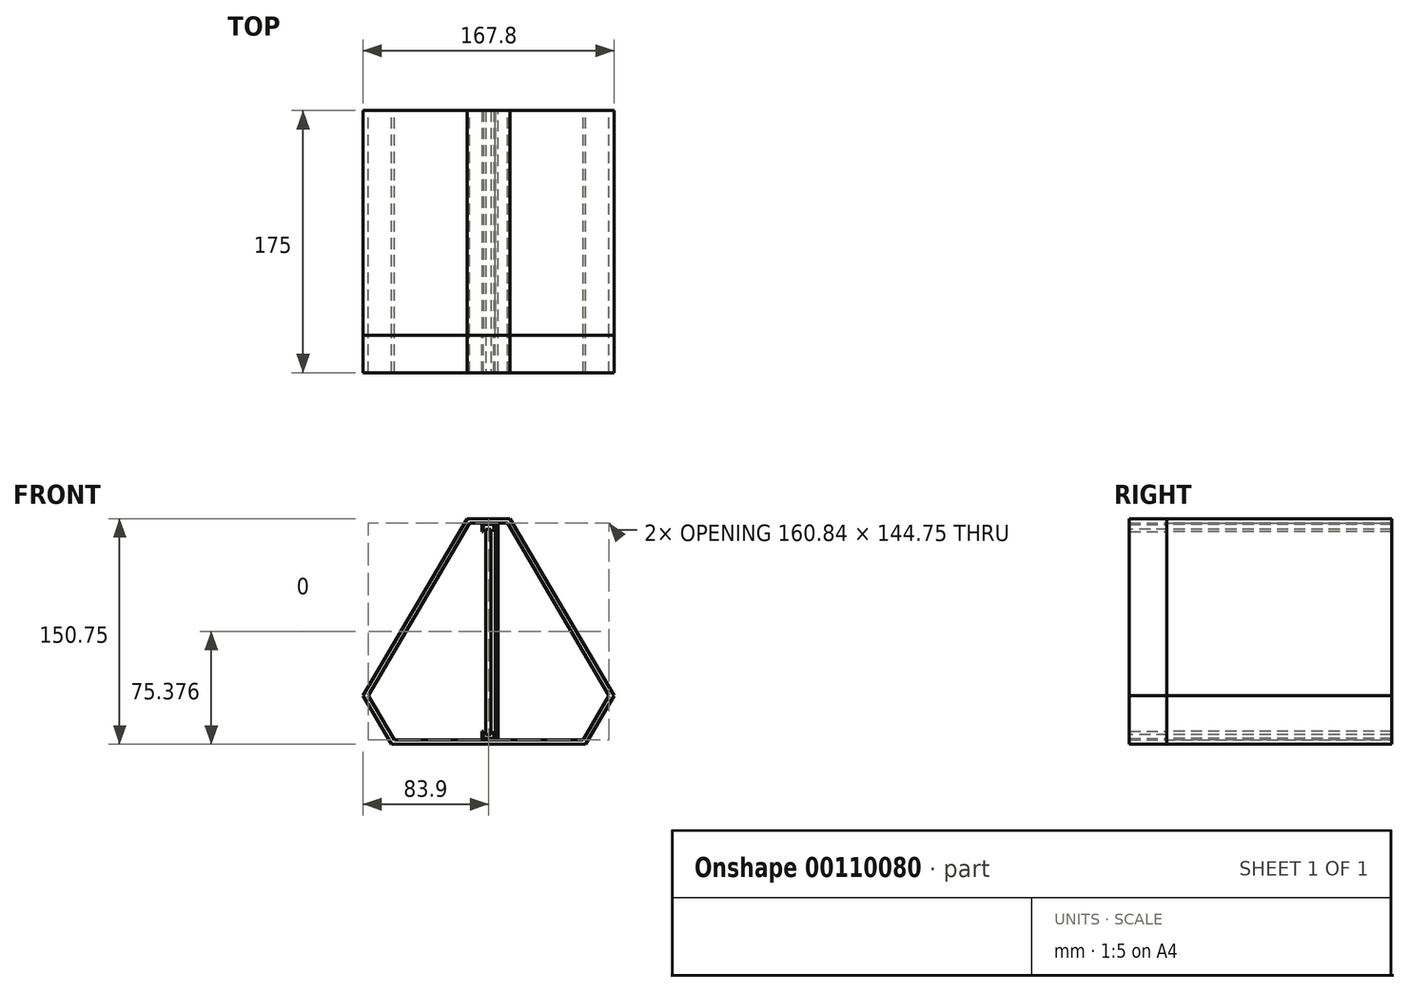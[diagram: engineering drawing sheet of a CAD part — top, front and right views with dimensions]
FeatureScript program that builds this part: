
annotation { "Feature Type Name" : "Feature", "Feature Type Description" : "" }
export const myFeature = defineFeature(function(context is Context, id is Id, definition is map)
    precondition{}
    {
        {
            var Q0;
            Q0=qCreatedBy(makeId("Front.planeOp"),FACE);
            var sketch = newSketch(context, id + "F0", { "sketchPlane" : qUnion([Q0])});
            skLineSegment(sketch, "E0", {"start": v(-63.04, 0) * mm, "end": v(63.04, 0) * mm});
            skLineSegment(sketch, "E1", {"start": v(0, 0) * mm, "end": v(0, 166.28) * mm, "construction": true});
            skLineSegment(sketch, "E2", {"start": v(-80.42, 29.55) * mm, "end": v(-12.66, 144.75) * mm});
            skLineSegment(sketch, "E3", {"start": v(12.66, 144.75) * mm, "end": v(80.42, 29.55) * mm});
            skLineSegment(sketch, "E4", {"start": v(-12.66, 144.75) * mm, "end": v(12.66, 144.75) * mm});
            skLineSegment(sketch, "E5", {"start": v(-80.42, 29.55) * mm, "end": v(-80.42, 0) * mm, "construction": true});
            skLineSegment(sketch, "E6.MirrorCS", {"start": v(-63.04, 0) * mm, "end": v(-80.42, 29.55) * mm});
            skPoint(sketch, "E7.orphan", {"position": v(-148.18, 144.75) * mm});
            skPoint(sketch, "E8.orphan", {"position": v(-97.8, 0) * mm});
            skLineSegment(sketch, "E9.MirrorCS", {"start": v(63.04, 0) * mm, "end": v(80.42, 29.55) * mm});
            skLineSegment(sketch, "E10.0", {"start": v(-64.76, -3) * mm, "end": v(-83.9, 29.55) * mm});
            skLineSegment(sketch, "E10.1", {"start": v(-14.38, 147.75) * mm, "end": v(14.38, 147.75) * mm});
            skLineSegment(sketch, "E10.2", {"start": v(14.38, 147.75) * mm, "end": v(83.9, 29.55) * mm});
            skLineSegment(sketch, "E10.3", {"start": v(-83.9, 29.55) * mm, "end": v(-14.38, 147.75) * mm});
            skLineSegment(sketch, "E10.4", {"start": v(64.76, -3) * mm, "end": v(83.9, 29.55) * mm});
            skLineSegment(sketch, "E10.5", {"start": v(-64.76, -3) * mm, "end": v(64.76, -3) * mm});
            skSolve(sketch);
        }
        {
            var Q0;
            Q0=makeQuery(id+"F0.imprint","IMPRINT",FACE,{"disambiguationData":[TD([[makeQuery(id+"F0.imprint","IMPRINT",EDGE,{"derivedFrom":sQuery(id+"F0.wireOp",EDGE,"E0")}),-1.0]])]});
            extrude(context, id + "F1", {"entities" : qUnion([Q0]), "depth" : 150 * mm});
        }
        {
            var Q0;
            Q0=makeQuery(id+"F1.opExtrude","CAP_FACE",FACE,{"disambiguationData":[OSD([sQuery(id+"F0.wireOp",EDGE,"E0"),sQuery(id+"F0.wireOp",EDGE,"E2"),sQuery(id+"F0.wireOp",EDGE,"E3"),sQuery(id+"F0.wireOp",EDGE,"E4"),sQuery(id+"F0.wireOp",EDGE,"E6.MirrorCS"),sQuery(id+"F0.wireOp",EDGE,"E9.MirrorCS"),sQuery(id+"F0.wireOp",EDGE,"E10.0"),sQuery(id+"F0.wireOp",EDGE,"E10.1"),sQuery(id+"F0.wireOp",EDGE,"E10.2"),sQuery(id+"F0.wireOp",EDGE,"E10.3"),sQuery(id+"F0.wireOp",EDGE,"E10.4"),sQuery(id+"F0.wireOp",EDGE,"E10.5")])],"isStart":false});
            var sketch = newSketch(context, id + "F2", { "sketchPlane" : qUnion([Q0])});
            skLineSegment(sketch, "E11", {"start": v(-4.43, 5.71) * mm, "end": v(-4.43, 0) * mm});
            skLineSegment(sketch, "E12", {"start": v(-4.43, 0) * mm, "end": v(0, 0) * mm});
            skLineSegment(sketch, "E13", {"start": v(0, 0) * mm, "end": v(0, 1.08) * mm});
            skLineSegment(sketch, "E14", {"start": v(0, 1.08) * mm, "end": v(-3.4, 1.08) * mm});
            skLineSegment(sketch, "E15", {"start": v(-3.4, 1.08) * mm, "end": v(-3.4, 5.71) * mm});
            skLineSegment(sketch, "E16", {"start": v(-3.4, 5.71) * mm, "end": v(-4.43, 5.71) * mm});
            skLineSegment(sketch, "E17.MirrorCS", {"start": v(3.4, 5.71) * mm, "end": v(4.43, 5.71) * mm});
            skLineSegment(sketch, "E18.MirrorCS", {"start": v(4.43, 5.71) * mm, "end": v(4.43, 0) * mm});
            skLineSegment(sketch, "E19.MirrorCS", {"start": v(3.4, 1.08) * mm, "end": v(3.4, 5.71) * mm});
            skLineSegment(sketch, "E20.MirrorCS", {"start": v(0, 1.08) * mm, "end": v(3.4, 1.08) * mm});
            skLineSegment(sketch, "E21.MirrorCS", {"start": v(4.43, 0) * mm, "end": v(0, 0) * mm});
            skPoint(sketch, "E22.orphan", {"position": v(-9.84, 5.71) * mm});
            skPoint(sketch, "E23.orphan", {"position": v(9.84, 5.71) * mm});
            skLineSegment(sketch, "E24", {"start": v(0, 144.75) * mm, "end": v(0, 0) * mm, "construction": true});
            skLineSegment(sketch, "E25", {"start": v(0, 72.38) * mm, "end": v(-93.7, 72.38) * mm, "construction": true});
            skLineSegment(sketch, "E26.MirrorCS", {"start": v(-3.4, 139.04) * mm, "end": v(-4.43, 139.04) * mm});
            skLineSegment(sketch, "E27.MirrorCS", {"start": v(-4.43, 139.04) * mm, "end": v(-4.43, 144.75) * mm});
            skLineSegment(sketch, "E28.MirrorCS", {"start": v(-3.4, 143.68) * mm, "end": v(-3.4, 139.04) * mm});
            skLineSegment(sketch, "E29.MirrorCS", {"start": v(0, 143.68) * mm, "end": v(-3.4, 143.68) * mm});
            skLineSegment(sketch, "E30.MirrorCS", {"start": v(-4.43, 144.75) * mm, "end": v(0, 144.75) * mm});
            skLineSegment(sketch, "E31.MirrorCS", {"start": v(4.43, 144.75) * mm, "end": v(0, 144.75) * mm});
            skLineSegment(sketch, "E32.MirrorCS", {"start": v(0, 143.68) * mm, "end": v(3.4, 143.68) * mm});
            skLineSegment(sketch, "E33.MirrorCS", {"start": v(3.4, 143.68) * mm, "end": v(3.4, 139.04) * mm});
            skLineSegment(sketch, "E34.MirrorCS", {"start": v(3.4, 139.04) * mm, "end": v(4.43, 139.04) * mm});
            skLineSegment(sketch, "E35.MirrorCS", {"start": v(4.43, 139.04) * mm, "end": v(4.43, 144.75) * mm});
            skSolve(sketch);
        }
        {
            var Q0;
            {var subQ0=sQuery(id+"F2.wireOp",EDGE,"E11");Q0=makeQuery(id+"F2.imprint","IMPRINT",FACE,{"disambiguationData":[TD([[makeQuery(id+"F2.imprint","IMPRINT",EDGE,{"derivedFrom":subQ0}),1.0]])]});}
            var Q1;
            Q1=makeQuery(id+"F2.imprint","IMPRINT",FACE,{"disambiguationData":[TD([[makeQuery(id+"F2.imprint","IMPRINT",EDGE,{"derivedFrom":sQuery(id+"F2.wireOp",EDGE,"E13")}),-1.0]])]});
            var Q2;
            Q2=makeQuery(id+"F2.imprint","IMPRINT",FACE,{"disambiguationData":[TD([[makeQuery(id+"F2.imprint","IMPRINT",EDGE,{"derivedFrom":sQuery(id+"F2.wireOp",EDGE,"E26.MirrorCS")}),-1.0]])]});
            extrude(context, id + "F3", {"entities" : qUnion([Q0, Q1, Q2]), "oppositeDirection" : true, "depth" : 150 * mm});
        }
        {
            var Q0;
            Q0=makeQuery(id+"F3.boolean.opBoolean","MERGE",FACE,{"derivedFrom":[makeQuery(id+"F1.opExtrude","CAP_FACE",FACE,{"disambiguationData":[OSD([sQuery(id+"F0.wireOp",EDGE,"E0"),sQuery(id+"F0.wireOp",EDGE,"E2"),sQuery(id+"F0.wireOp",EDGE,"E3"),sQuery(id+"F0.wireOp",EDGE,"E4"),sQuery(id+"F0.wireOp",EDGE,"E6.MirrorCS"),sQuery(id+"F0.wireOp",EDGE,"E9.MirrorCS"),sQuery(id+"F0.wireOp",EDGE,"E10.0"),sQuery(id+"F0.wireOp",EDGE,"E10.1"),sQuery(id+"F0.wireOp",EDGE,"E10.2"),sQuery(id+"F0.wireOp",EDGE,"E10.3"),sQuery(id+"F0.wireOp",EDGE,"E10.4"),sQuery(id+"F0.wireOp",EDGE,"E10.5")])],"isStart":false}),makeQuery(id+"F3.opExtrude","CAP_FACE",FACE,{"disambiguationData":[OSD([sQuery(id+"F2.wireOp",EDGE,"E11"),sQuery(id+"F2.wireOp",EDGE,"E12"),sQuery(id+"F2.wireOp",EDGE,"E14"),sQuery(id+"F2.wireOp",EDGE,"E15"),sQuery(id+"F2.wireOp",EDGE,"E16"),sQuery(id+"F2.wireOp",EDGE,"E17.MirrorCS"),sQuery(id+"F2.wireOp",EDGE,"E18.MirrorCS"),sQuery(id+"F2.wireOp",EDGE,"E19.MirrorCS"),sQuery(id+"F2.wireOp",EDGE,"E20.MirrorCS"),sQuery(id+"F2.wireOp",EDGE,"E21.MirrorCS")])],"isStart":true}),makeQuery(id+"F3.opExtrude","CAP_FACE",FACE,{"disambiguationData":[OSD([sQuery(id+"F2.wireOp",EDGE,"E26.MirrorCS"),sQuery(id+"F2.wireOp",EDGE,"E27.MirrorCS"),sQuery(id+"F2.wireOp",EDGE,"E28.MirrorCS"),sQuery(id+"F2.wireOp",EDGE,"E29.MirrorCS"),sQuery(id+"F2.wireOp",EDGE,"E30.MirrorCS"),sQuery(id+"F2.wireOp",EDGE,"E31.MirrorCS"),sQuery(id+"F2.wireOp",EDGE,"E32.MirrorCS"),sQuery(id+"F2.wireOp",EDGE,"E33.MirrorCS"),sQuery(id+"F2.wireOp",EDGE,"E34.MirrorCS"),sQuery(id+"F2.wireOp",EDGE,"E35.MirrorCS")])],"isStart":true})]});
            extrude(context, id + "F4", {"entities" : qUnion([Q0]), "depth" : 25 * mm});
        }
        {
            var Q0;
            Q0=makeQuery(id+"F4.opExtrude","CAP_FACE",FACE,{"disambiguationData":[OSD([sQuery(id+"F0.wireOp",EDGE,"E0"),sQuery(id+"F0.wireOp",EDGE,"E2"),sQuery(id+"F0.wireOp",EDGE,"E3"),sQuery(id+"F0.wireOp",EDGE,"E4"),sQuery(id+"F0.wireOp",EDGE,"E6.MirrorCS"),sQuery(id+"F0.wireOp",EDGE,"E9.MirrorCS"),sQuery(id+"F0.wireOp",EDGE,"E10.0"),sQuery(id+"F0.wireOp",EDGE,"E10.1"),sQuery(id+"F0.wireOp",EDGE,"E10.2"),sQuery(id+"F0.wireOp",EDGE,"E10.3"),sQuery(id+"F0.wireOp",EDGE,"E10.4"),sQuery(id+"F0.wireOp",EDGE,"E10.5"),sQuery(id+"F2.wireOp",EDGE,"E11"),sQuery(id+"F2.wireOp",EDGE,"E12"),sQuery(id+"F2.wireOp",EDGE,"E14"),sQuery(id+"F2.wireOp",EDGE,"E15"),sQuery(id+"F2.wireOp",EDGE,"E16"),sQuery(id+"F2.wireOp",EDGE,"E17.MirrorCS"),sQuery(id+"F2.wireOp",EDGE,"E18.MirrorCS"),sQuery(id+"F2.wireOp",EDGE,"E19.MirrorCS"),sQuery(id+"F2.wireOp",EDGE,"E20.MirrorCS"),sQuery(id+"F2.wireOp",EDGE,"E21.MirrorCS"),sQuery(id+"F2.wireOp",EDGE,"E26.MirrorCS"),sQuery(id+"F2.wireOp",EDGE,"E27.MirrorCS"),sQuery(id+"F2.wireOp",EDGE,"E28.MirrorCS"),sQuery(id+"F2.wireOp",EDGE,"E29.MirrorCS"),sQuery(id+"F2.wireOp",EDGE,"E30.MirrorCS"),sQuery(id+"F2.wireOp",EDGE,"E31.MirrorCS"),sQuery(id+"F2.wireOp",EDGE,"E32.MirrorCS"),sQuery(id+"F2.wireOp",EDGE,"E33.MirrorCS"),sQuery(id+"F2.wireOp",EDGE,"E34.MirrorCS"),sQuery(id+"F2.wireOp",EDGE,"E35.MirrorCS")])],"isStart":false});
            var sketch = newSketch(context, id + "F5", { "sketchPlane" : qUnion([Q0])});
            skPoint(sketch, "E36.oppositeSnap0", {"position": v(3.4, 3.4) * mm});
            skLineSegment(sketch, "E36.bottom", {"start": v(-1.8, 140.78) * mm, "end": v(1.61, 140.78) * mm});
            skLineSegment(sketch, "E36.top", {"start": v(-1.8, 3.4) * mm, "end": v(1.61, 3.4) * mm});
            skLineSegment(sketch, "E36.left", {"start": v(-1.8, 140.78) * mm, "end": v(-1.8, 3.4) * mm});
            skLineSegment(sketch, "E36.right", {"start": v(1.61, 140.78) * mm, "end": v(1.61, 3.4) * mm});
            skSolve(sketch);
        }
        {
            var Q0;
            Q0 = qSketchRegion(id + "F5", true);
            extrude(context, id + "F6", {"entities" : qUnion([Q0]), "oppositeDirection" : true, "depth" : 175 * mm});
        }
        {
            var Q0;
            Q0=makeQuery(id+"F1.opExtrude","CAP_FACE",FACE,{"disambiguationData":[OSD([sQuery(id+"F0.wireOp",EDGE,"E0"),sQuery(id+"F0.wireOp",EDGE,"E2"),sQuery(id+"F0.wireOp",EDGE,"E3"),sQuery(id+"F0.wireOp",EDGE,"E4"),sQuery(id+"F0.wireOp",EDGE,"E6.MirrorCS"),sQuery(id+"F0.wireOp",EDGE,"E9.MirrorCS"),sQuery(id+"F0.wireOp",EDGE,"E10.0"),sQuery(id+"F0.wireOp",EDGE,"E10.1"),sQuery(id+"F0.wireOp",EDGE,"E10.2"),sQuery(id+"F0.wireOp",EDGE,"E10.3"),sQuery(id+"F0.wireOp",EDGE,"E10.4"),sQuery(id+"F0.wireOp",EDGE,"E10.5")])],"isStart":true});
            var sketch = newSketch(context, id + "F7", { "sketchPlane" : qUnion([Q0])});
            skLineSegment(sketch, "E37.bottom", {"start": v(-4.43, 144.75) * mm, "end": v(-6.43, 144.75) * mm});
            skLineSegment(sketch, "E37.top", {"start": v(-4.43, 0) * mm, "end": v(-6.43, 0) * mm});
            skLineSegment(sketch, "E37.left", {"start": v(-4.43, 144.75) * mm, "end": v(-4.43, 0) * mm});
            skLineSegment(sketch, "E37.right", {"start": v(-6.43, 144.75) * mm, "end": v(-6.43, 0) * mm});
            skSolve(sketch);
        }
        {
            var Q0;
            Q0 = qSketchRegion(id + "F7", true);
            var Q1;
            Q1=makeQuery(id+"F4.opExtrude","CAP_FACE",FACE,{"disambiguationData":[OSD([sQuery(id+"F0.wireOp",EDGE,"E0"),sQuery(id+"F0.wireOp",EDGE,"E2"),sQuery(id+"F0.wireOp",EDGE,"E3"),sQuery(id+"F0.wireOp",EDGE,"E4"),sQuery(id+"F0.wireOp",EDGE,"E6.MirrorCS"),sQuery(id+"F0.wireOp",EDGE,"E9.MirrorCS"),sQuery(id+"F0.wireOp",EDGE,"E10.0"),sQuery(id+"F0.wireOp",EDGE,"E10.1"),sQuery(id+"F0.wireOp",EDGE,"E10.2"),sQuery(id+"F0.wireOp",EDGE,"E10.3"),sQuery(id+"F0.wireOp",EDGE,"E10.4"),sQuery(id+"F0.wireOp",EDGE,"E10.5")])],"isStart":false});
            extrude(context, id + "F8", {"entities" : qUnion([Q0]), "endBound" : BoundingType.UP_TO_SURFACE, "oppositeDirection" : true, "endBoundEntityFace" : qUnion([Q1]), "depth" : 25 * mm});
        }
    });
